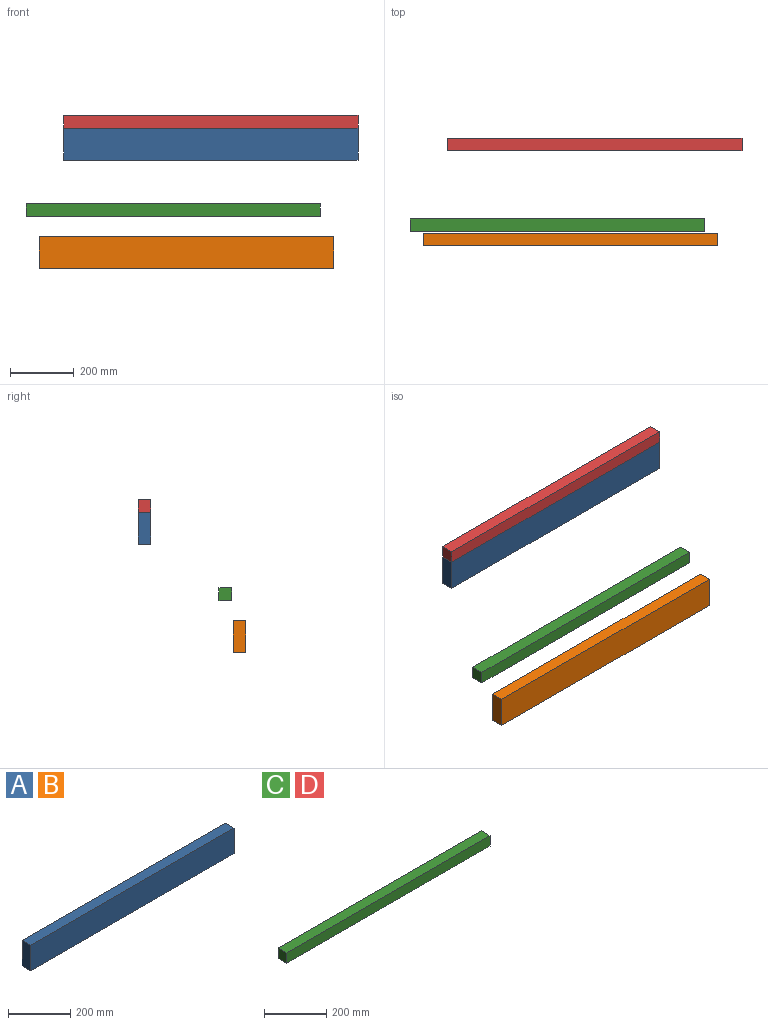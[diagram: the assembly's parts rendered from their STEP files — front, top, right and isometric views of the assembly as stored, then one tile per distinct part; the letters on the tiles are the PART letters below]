
ASSEMBLY  parts=4 mates=1
PART A: 6 faces, bbox 920x40x100 mm
  f0: plane 100x40mm, normal (1,0,0), area 4000mm2, adj f1,f3,f4,f5
  f1: plane 920x100mm, normal (0,1,0), area 92000mm2, adj f0,f2,f4,f5
  f2: plane 100x40mm, normal (-1,0,0), area 4000mm2, adj f1,f3,f4,f5
  f3: plane 920x100mm, normal (0,-1,0), area 92000mm2, adj f0,f2,f4,f5
  f4: plane 920x40mm, normal (0,0,-1), area 36800mm2, adj f0,f1,f2,f3
  f5: plane 920x40mm, normal (0,0,1), area 36800mm2, adj f0,f1,f2,f3
PART B: same geometry as A
PART C: 6 faces, bbox 920x40x40 mm
  f0: plane 40x40mm, normal (1,0,0), area 1600mm2, adj f1,f3,f4,f5
  f1: plane 920x40mm, normal (0,1,0), area 36800mm2, adj f0,f2,f4,f5
  f2: plane 40x40mm, normal (-1,0,0), area 1600mm2, adj f1,f3,f4,f5
  f3: plane 920x40mm, normal (0,-1,0), area 36800mm2, adj f0,f2,f4,f5
  f4: plane 920x40mm, normal (0,0,-1), area 36800mm2, adj f0,f1,f2,f3
  f5: plane 920x40mm, normal (0,0,1), area 36800mm2, adj f0,f1,f2,f3
PART D: same geometry as C
PLACE A t=(-23.38,114.26,151.63)mm
PLACE B t=(-99.72,-182.36,-187.18)mm
PLACE C t=(-141.94,-138.4,-84.67)mm
PLACE D t=(-23.38,114.26,191.63)mm
MATE planar A.f5 <-> D.f4  axis (0,0,1) through (-23.38,114.26,151.63)mm
